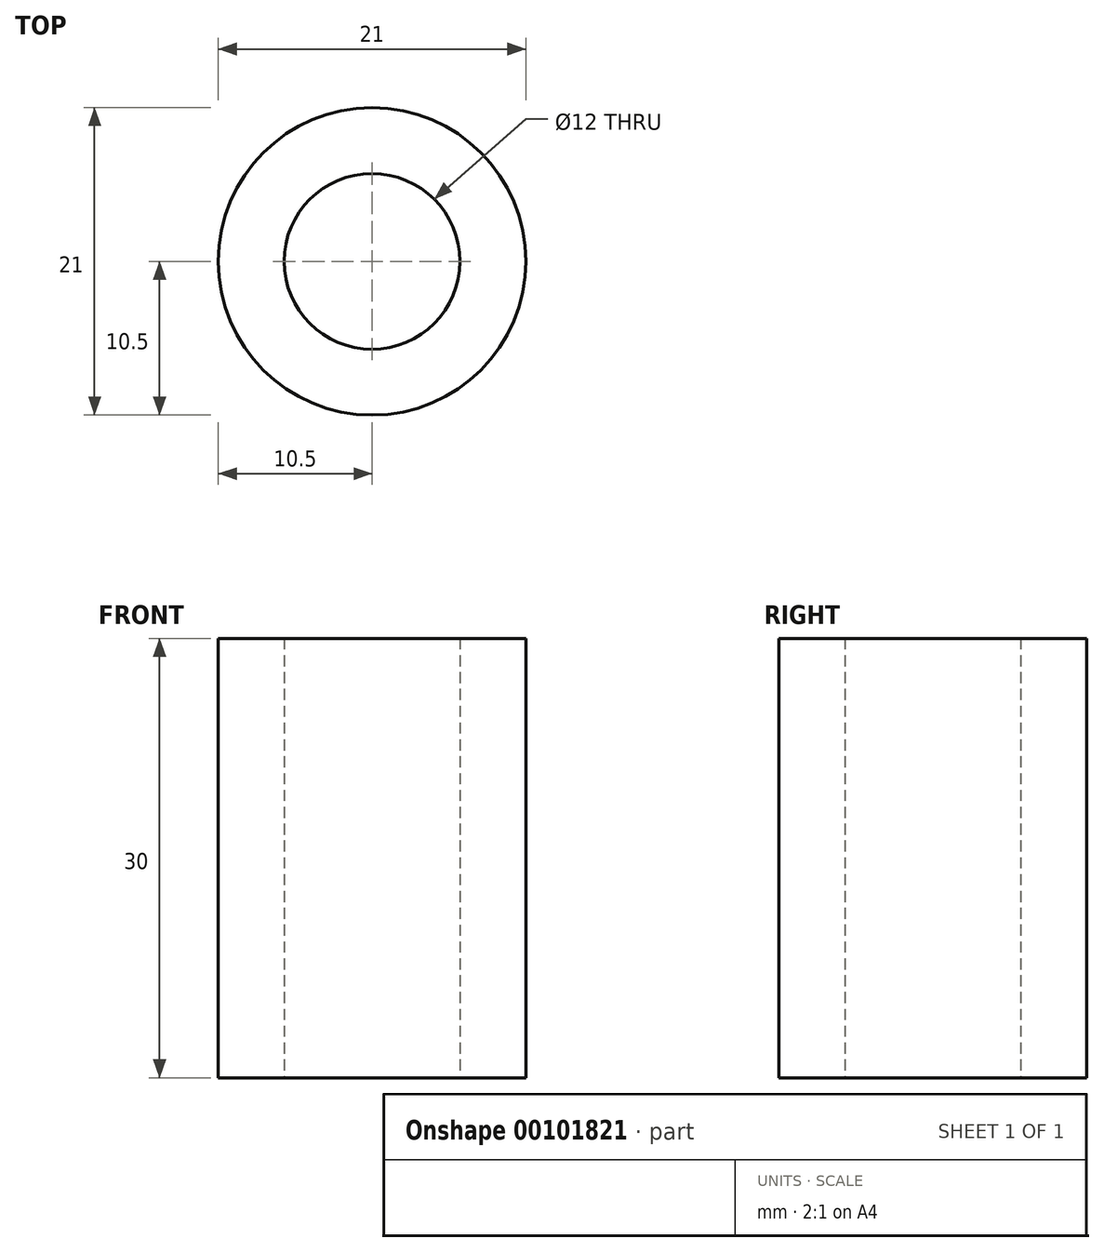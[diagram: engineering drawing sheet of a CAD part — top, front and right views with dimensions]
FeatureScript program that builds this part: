
annotation { "Feature Type Name" : "Feature", "Feature Type Description" : "" }
export const myFeature = defineFeature(function(context is Context, id is Id, definition is map)
    precondition{}
    {
        {
            var Q0;
            Q0=qCreatedBy(makeId("Top.planeOp"),FACE);
            var sketch = newSketch(context, id + "F0", { "sketchPlane" : qUnion([Q0])});
            skCircle(sketch, "E0", {"center": v(0, 0) * mm, "radius": 6 * mm});
            skCircle(sketch, "E1", {"center": v(0, 0) * mm, "radius": 10.5 * mm});
            skSolve(sketch);
        }
        {
            var Q0;
            Q0=makeQuery(id+"F0.imprint","IMPRINT",FACE,{"disambiguationData":[TD([[makeQuery(id+"F0.imprint","IMPRINT",EDGE,{"derivedFrom":sQuery(id+"F0.wireOp",EDGE,"E0")}),-1.0]])]});
            extrude(context, id + "F1", {"entities" : qUnion([Q0]), "depth" : 30 * mm});
        }
    });
